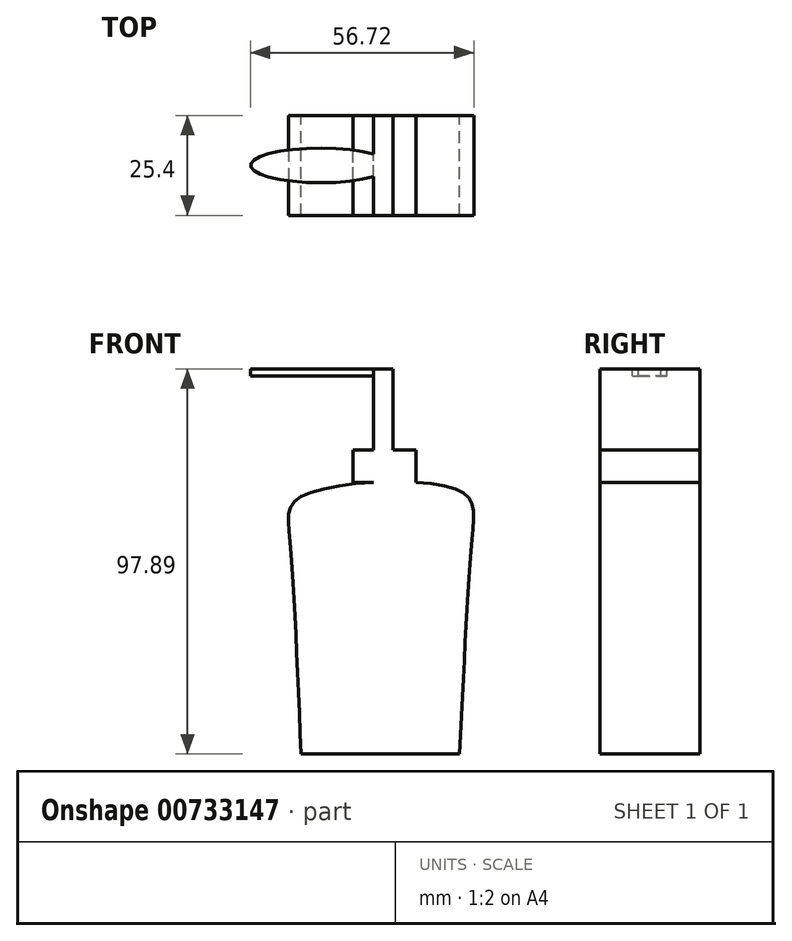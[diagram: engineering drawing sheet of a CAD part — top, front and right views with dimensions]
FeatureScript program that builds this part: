
annotation { "Feature Type Name" : "Feature", "Feature Type Description" : "" }
export const myFeature = defineFeature(function(context is Context, id is Id, definition is map)
    precondition{}
    {
        {
            var Q0;
            Q0=qCreatedBy(makeId("Front.planeOp"),FACE);
            var sketch = newSketch(context, id + "F0", { "sketchPlane" : qUnion([Q0])});
            skLineSegment(sketch, "E0", {"start": v(-20.88, -55.63) * mm, "end": v(19.42, -55.63) * mm});
            skFitSpline(sketch, "E1", {"points": [v(-20.88, -55.63) * mm, v(-23.8, 0) * mm, v(-20.88, 9.78) * mm, v(19.42, 11.24) * mm, v(22.63, 0) * mm, v(19.42, -55.63) * mm], "startDerivative": vector(-10.47, 248.48) * mm, "endDerivative": vector(-11.55, -243.57) * mm});
            skLineSegment(sketch, "E2.bottom", {"start": v(-7.74, 21.7) * mm, "end": v(8.35, 21.7) * mm});
            skLineSegment(sketch, "E2.top", {"start": v(-7.74, 13.45) * mm, "end": v(8.35, 13.45) * mm});
            skLineSegment(sketch, "E2.left", {"start": v(-7.74, 21.7) * mm, "end": v(-7.74, 13.45) * mm});
            skLineSegment(sketch, "E2.right", {"start": v(8.35, 21.7) * mm, "end": v(8.35, 13.45) * mm});
            skLineSegment(sketch, "E3.bottom", {"start": v(2.48, 21.7) * mm, "end": v(-2.48, 21.7) * mm});
            skLineSegment(sketch, "E3.top", {"start": v(2.48, 42.26) * mm, "end": v(-2.48, 42.26) * mm});
            skLineSegment(sketch, "E3.left", {"start": v(2.48, 21.7) * mm, "end": v(2.48, 42.26) * mm});
            skLineSegment(sketch, "E3.right", {"start": v(-2.48, 21.7) * mm, "end": v(-2.48, 42.26) * mm});
            skPoint(sketch, "E3.middle", {"position": v(0, 31.97) * mm});
            skSolve(sketch);
        }
        {
            var Q0;
            {var subQ0=sQuery(id+"F0.wireOp",EDGE,"E2.top");var subQ1=sQuery(id+"F0.wireOp",EDGE,"E1");var subQ3=makeQuery(id+"F0.imprint","INTERSECT",VERTEX,{"derivedFrom":[subQ1,subQ0]});Q0=makeQuery(id+"F0.imprint","IMPRINT",FACE,{"disambiguationData":[TD([[makeQuery(id+"F0.imprint","IMPRINT",EDGE,{"disambiguationData":[TD([[subQ3,-1.0]])],"derivedFrom":subQ1}),-1.0]])]});}
            extrude(context, id + "F1", {"entities" : qUnion([Q0]), "depth" : 25.4 * mm, "offsetDistance" : 25.4 * mm});
        }
        {
            var Q0;
            Q0 = qSketchRegion(id + "F0", true);
            extrude(context, id + "F2", {"entities" : qUnion([Q0]), "operationType" : NewBodyOperationType.ADD, "depth" : 25.4 * mm, "offsetDistance" : 25.4 * mm});
        }
        {
            var Q0;
            Q0=makeQuery(id+"F2.opExtrude","SWEPT_FACE",FACE,{"disambiguationData":[OSD([sQuery(id+"F0.wireOp",EDGE,"E3.top")])]});
            var sketch = newSketch(context, id + "F3", { "sketchPlane" : qUnion([Q0])});
            skEllipse(sketch, "E4", {"center": v(-15.91, -12.7) * mm, "majorRadius": 17.81 * mm, "minorRadius": 4.42 * mm, "majorAxis": v(1, 0)});
            skPoint(sketch, "E4.centerSnap0", {"position": v(-2.48, -12.7) * mm});
            skSolve(sketch);
        }
        {
            var Q0;
            Q0 = qSketchRegion(id + "F3", true);
            extrude(context, id + "F4", {"entities" : qUnion([Q0]), "operationType" : NewBodyOperationType.ADD, "oppositeDirection" : true, "depth" : 1.78 * mm, "offsetDistance" : 25.4 * mm});
        }
    });
